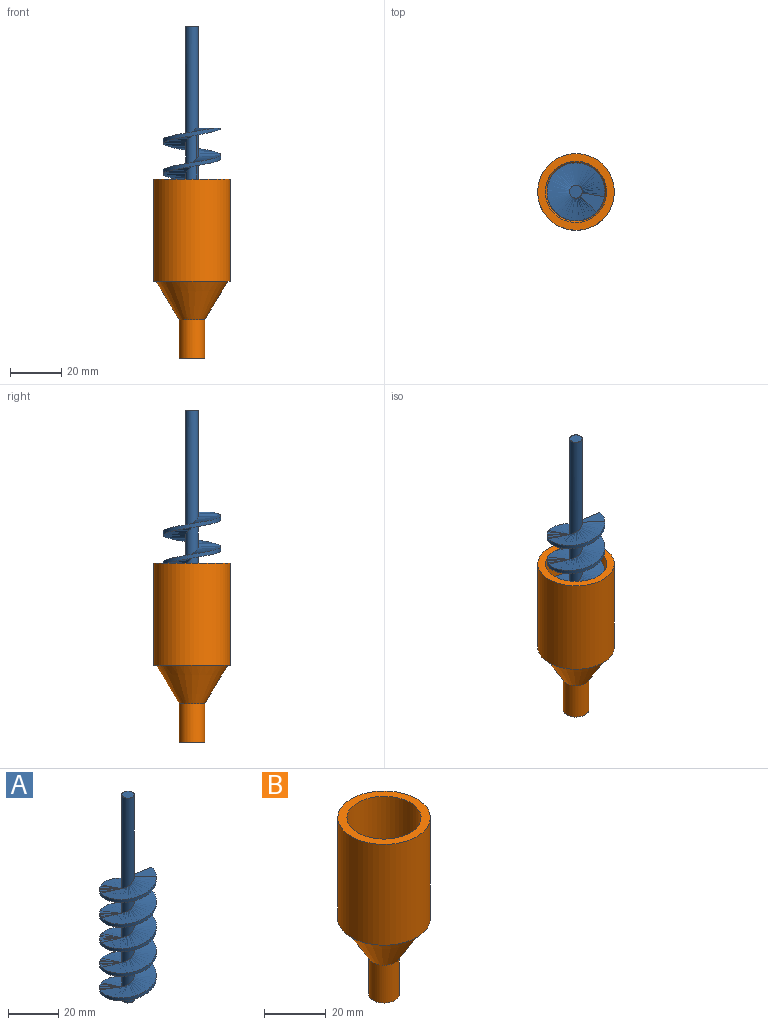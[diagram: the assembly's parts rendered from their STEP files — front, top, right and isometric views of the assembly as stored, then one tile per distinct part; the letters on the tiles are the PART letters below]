
ASSEMBLY  parts=2 mates=1
PART A: 14 faces, bbox 23.9x23.9x100 mm
  f0: plane 8.69x1.53mm, normal (-0.17,-0.98,0), area 10.3mm2, adj f2,f4,f5,f7
  f1: bspline ~59.67x22.64mm, area 1979.5mm2, adj f2,f3,f5,f7,f8,f9,f10,f11
  f2: cylinder r=11.33mm len=60mm, axis (0,0,-1), area 752.1mm2, adj f0,f1,f3,f4,f5,f6
  f3: plane 8.69x1.53mm, normal (0.17,0.98,0), area 2.9mm2, adj f1,f2,f6,f11
  f4: bspline ~60x23.94mm, area 1960.6mm2, adj f0,f2,f6,f7,f8,f9,f10,f11
  f5: plane 13.83x5mm, normal (0,0,-1), area 30.5mm2, adj f0,f1,f2,f7,f12
  f6: plane 9.38x7.54mm, normal (0,0,1), area 37mm2, adj f2,f3,f4,f11
  f7: cylinder r=2.5mm len=22.5mm, axis (0,0,-1), area 165.8mm2, adj f0,f1,f4,f5,f8,f12
  f8: cylinder r=2.5mm len=22.5mm, axis (0,0,-1), area 164.9mm2, adj f1,f4,f7,f9
  f9: cylinder r=2.5mm len=22.5mm, axis (0,0,-1), area 164.9mm2, adj f1,f4,f8,f10
  f10: cylinder r=2.5mm len=22.5mm, axis (0,0,-1), area 164.9mm2, adj f1,f4,f9,f11
  f11: cylinder r=2.5mm len=52mm, axis (0,0,-1), area 721.2mm2, adj f1,f3,f4,f6,f10,f13
  f12: cylinder r=2.5mm len=10.5mm, axis (0,0,-1), area 72.2mm2, adj f1,f5,f7
  f13: plane 5x5mm, normal (0,0,1), area 19.6mm2, adj f11
PART B: 11 faces, bbox 30x30x70 mm
  f0: cylinder r=3mm len=6mm, axis (0,0,1), area 106.8mm2, adj f1,f6
  f1: plane 10x10mm, normal (0,0,-1), area 50.3mm2, adj f0,f2
  f2: cylinder r=5mm len=15mm, axis (0,0,1), area 471.2mm2, adj f1,f3
  f3: cone r=14mm half-angle=31deg, axis (0,0,1), area 1044.2mm2, adj f2,f7
  f4: cone r=3mm half-angle=31deg, axis (0,0,1), area 824.3mm2, adj f5,f9
  f5: cone r=3mm half-angle=12.1deg, axis (0,0,1), area 120mm2, adj f4,f6
  f6: plane 6x6mm, normal (0,0,-1), area 25.1mm2, adj f0,f5
  f7: plane 30x30mm, normal (0,0,-1), area 91.1mm2, adj f3,f10
  f8: plane 30x30mm, normal (0,0,1), area 254.5mm2, adj f9,f10
  f9: cylinder r=12mm len=40mm, axis (0,0,1), area 3015.9mm2, adj f4,f8
  f10: cylinder r=15mm len=40mm, axis (0,0,1), area 3769.9mm2, adj f7,f8
PLACE A t=(-0.01,0.02,-13.5)mm
PLACE B t=(-15.01,20.02,-13.5)mm
MATE revolute A.f7 <-> B.f0  axis (0,0,-1) through (-0.01,0.02,-13.5)mm
